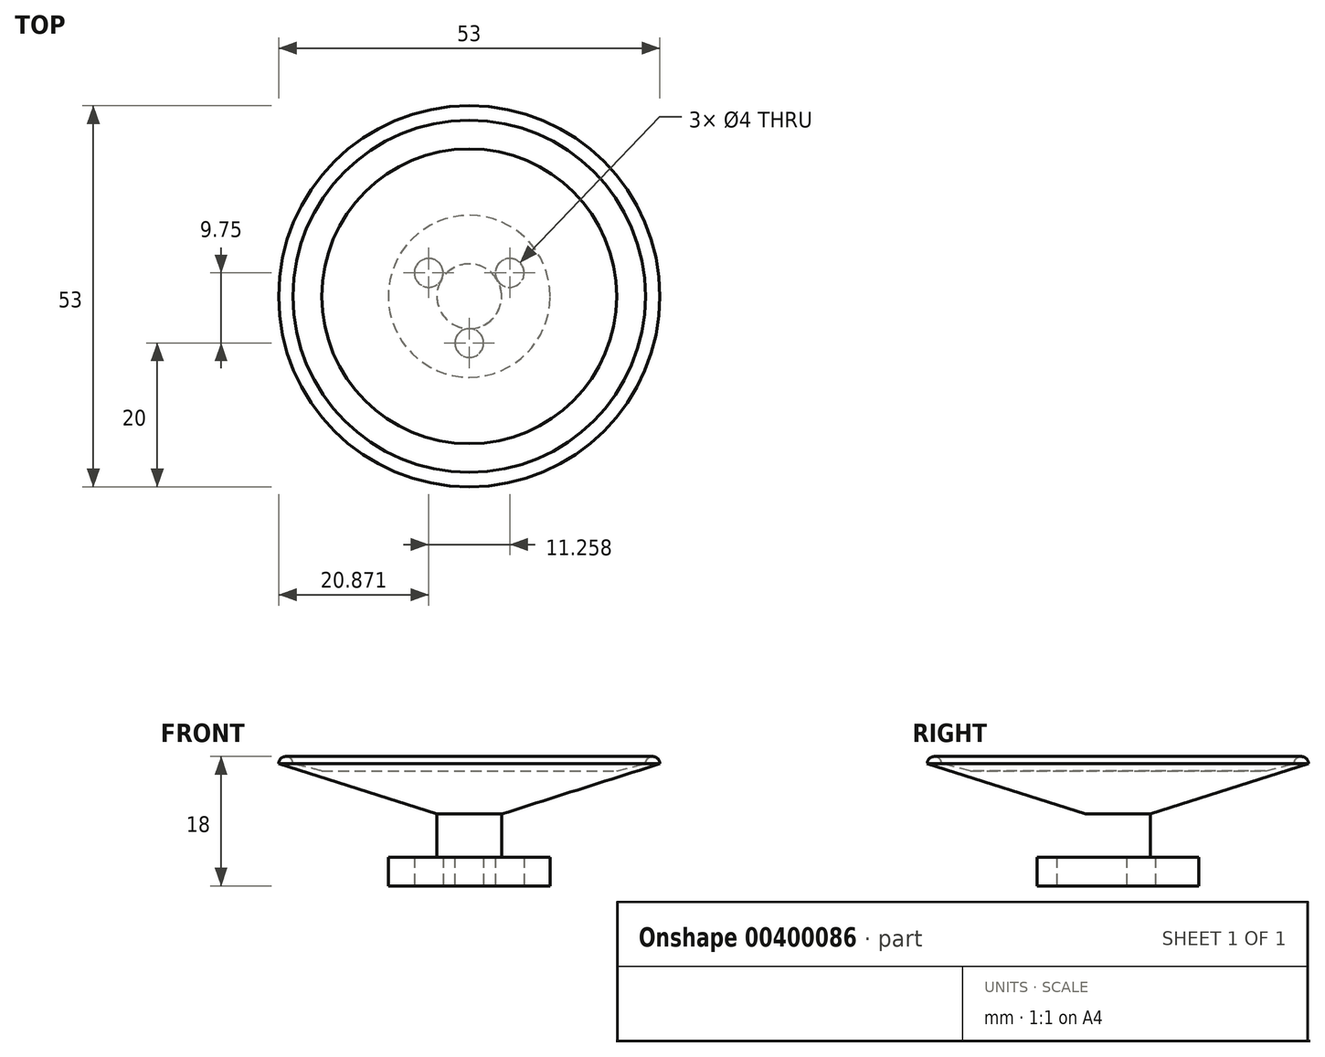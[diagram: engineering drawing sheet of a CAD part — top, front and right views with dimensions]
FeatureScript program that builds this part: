
annotation { "Feature Type Name" : "Feature", "Feature Type Description" : "" }
export const myFeature = defineFeature(function(context is Context, id is Id, definition is map)
    precondition{}
    {
        {
            var Q0;
            Q0=qCreatedBy(makeId("Top.planeOp"),FACE);
            var sketch = newSketch(context, id + "F0", { "sketchPlane" : qUnion([Q0])});
            skCircle(sketch, "E0", {"center": v(0, 0) * mm, "radius": 11.25 * mm});
            skSolve(sketch);
        }
        {
            var Q0;
            Q0=qSketchRegion(id+"F0",true);
            extrude(context, id + "F1", {"entities" : qUnion([Q0]), "depth" : 4 * mm});
        }
        {
            var Q0;
            Q0=makeQuery(id+"F1.opExtrude","CAP_FACE",FACE,{"disambiguationData":[OSD([sQuery(id+"F0.wireOp",EDGE,"E0")])],"isStart":false});
            var sketch = newSketch(context, id + "F2", { "sketchPlane" : qUnion([Q0])});
            skCircle(sketch, "E1", {"center": v(0, 0) * mm, "radius": 4.5 * mm});
            skSolve(sketch);
        }
        {
            var Q0;
            Q0=qSketchRegion(id+"F2",true);
            extrude(context, id + "F3", {"entities" : qUnion([Q0]), "operationType" : NewBodyOperationType.ADD, "depth" : 6 * mm});
        }
        {
            var Q0;
            Q0=qCreatedBy(makeId("Front.planeOp"),FACE);
            var sketch = newSketch(context, id + "F4", { "sketchPlane" : qUnion([Q0])});
            skLineSegment(sketch, "E2", {"start": v(0, 16) * mm, "end": v(20.5, 16) * mm});
            skLineSegment(sketch, "E3", {"start": v(20.5, 16) * mm, "end": v(24.5, 17) * mm});
            skLineSegment(sketch, "E4.0", {"start": v(0, 10) * mm, "end": v(4.5, 10) * mm});
            skLineSegment(sketch, "E5", {"start": v(4.5, 10) * mm, "end": v(26.5, 17) * mm});
            skLineSegment(sketch, "E6", {"start": v(0, 0) * mm, "end": v(0, 38.4) * mm, "construction": true});
            skLineSegment(sketch, "E7", {"start": v(24.5, 17) * mm, "end": v(26.5, 17) * mm, "construction": true});
            skArc(sketch, "E8", {"start": v(26.5, 17) * mm, "mid": v(25.5, 18) * mm, "end": v(24.5, 17) * mm});
            skLineSegment(sketch, "E9", {"start": v(21.34, 18) * mm, "end": v(29.98, 18) * mm, "construction": true});
            skLineSegment(sketch, "E10", {"start": v(0, 16) * mm, "end": v(0, 10) * mm});
            skSolve(sketch);
        }
        {
            var Q0;
            Q0=qSketchRegion(id+"F4",true);
            var Q1;
            Q1=sQuery(id+"F4.wireOp",EDGE,"E6");
            revolve(context, id + "F5", {"operationType" : NewBodyOperationType.ADD, "entities" : qUnion([Q0]), "axis" : qUnion([Q1]), "revolveType" : RevolveType.FULL});
        }
        {
            var Q0;
            Q0=makeQuery(id+"F1.opExtrude","CAP_FACE",FACE,{"disambiguationData":[OSD([sQuery(id+"F0.wireOp",EDGE,"E0")])],"isStart":true});
            var sketch = newSketch(context, id + "F6", { "sketchPlane" : qUnion([Q0])});
            skCircle(sketch, "E11", {"center": v(0, 6.5) * mm, "radius": 2 * mm});
            skCircle(sketch, "E12.1.0", {"center": v(-5.63, -3.25) * mm, "radius": 2 * mm});
            skCircle(sketch, "E12.2.0", {"center": v(5.63, -3.25) * mm, "radius": 2 * mm});
            skPoint(sketch, "E12.center", {"position": v(0, 0) * mm});
            skSolve(sketch);
        }
        {
            var Q0;
            Q0=makeQuery(id+"F6.imprint","IMPRINT",FACE,{"disambiguationData":[TD([[makeQuery(id+"F6.imprint","IMPRINT",EDGE,{"derivedFrom":sQuery(id+"F6.wireOp",EDGE,"E12.1.0")}),1.0]])]});
            var Q1;
            Q1=makeQuery(id+"F6.imprint","IMPRINT",FACE,{"disambiguationData":[TD([[makeQuery(id+"F6.imprint","IMPRINT",EDGE,{"derivedFrom":sQuery(id+"F6.wireOp",EDGE,"E12.2.0")}),1.0]])]});
            var Q2;
            Q2=makeQuery(id+"F6.imprint","IMPRINT",FACE,{"disambiguationData":[TD([[makeQuery(id+"F6.imprint","IMPRINT",EDGE,{"derivedFrom":sQuery(id+"F6.wireOp",EDGE,"E11")}),1.0]])]});
            var Q3;
            Q3=makeQuery(id+"F1.opExtrude","CAP_FACE",FACE,{"disambiguationData":[OSD([sQuery(id+"F0.wireOp",EDGE,"E0")])],"isStart":false});
            extrude(context, id + "F7", {"entities" : qUnion([Q0, Q1, Q2]), "operationType" : NewBodyOperationType.REMOVE, "endBound" : BoundingType.UP_TO_SURFACE, "oppositeDirection" : true, "endBoundEntityFace" : qUnion([Q3]), "depth" : 25 * mm});
        }
    });
